# Revit family: Kessel AG 28682 en
name_source: partatom
category: Sanitärinstallationen
revit_build: Autodesk Revit 2014 (Build: 20130308_1515(x64)
units: mm (PartAtom-declared; Revit-internal decimal feet)

## types (1)
- Kessel AG 28682 en
    <1.010.00.2> Number of the part of the guideline = 4
    <1.010.00.3> Issue date (month) of the guideline = 201805
    <1.010.00.4> Manufacturer name = Kessel AG
    <1.010.00.5> Revision date of the file = Kessel AG
    <1.800.00.3> BS number = 10000100000000000000000000000000000000000000000161000
    <1.800.00.4> Comment field = Absperreinrichtung DN 80, waagrecht
    <1.810.00.3> Manufacturer’s reference number = 28682
    <1.810.00.4> DATANORM number = 28682
    <4.100.00.4> Area of application = Zubehör
    <4.110.00.4> Model series = Zubehör
    <4.700.00.4> Product name = Absperreinrichtung DN 80, waagrecht
    <4.700.00.5> Type of connection = Gate valve DN 100, horizontally
    CONNECTOR0_ref_dZ = 1 mm  [stored 0.00328084 ft]
    CONNECTOR1_DIAMETER_dY_0r = 0 mm  [stored 0 ft]
    CONNECTOR1_dY_00 = 118 mm
    CONNECTOR1_dY_01 = 108 mm
    CONNECTOR1_ref_dY = 108 mm
    CONNECTOR1_ref_dZ = 71 mm  [stored 0.23294 ft]
    Hersteller = Kessel AG
    Modell = 28682

note: [stored X ft] marks values corroborated as IEEE doubles in the binary element streams (Revit-internal decimal feet)
